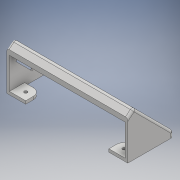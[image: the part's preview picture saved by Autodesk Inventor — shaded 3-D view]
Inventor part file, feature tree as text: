
AUTODESK INVENTOR PART (.ipt)
format: ipt  version: 2018 (Build 220112000, 112)  size: 429,056 bytes
history: native  units: mm
features: extrude x10, sketch x10, projected_geometry x3, fillet x2, chamfer x1, mirror x1, emboss x1
ambient origin geometry x8: Origin, YZ Plane, XZ Plane, XY Plane, X Axis, Y Axis, Z Axis, Center Point
bodies: Solid1 (feature_tree)
feature tree (28):
  extrude  "Extrusion1"  Depth=73.0mm
  extrude  "Extrusion2"  Depth=60.0mm
  extrude  "Extrusion3"  Depth=7.0mm
  fillet  "Fillet1"  Radius=3.5mm
  extrude  "Extrusion4"  Depth=3.5mm
  extrude  "Extrusion5"  Depth=120.0mm TaperAngle=0.0deg
  extrude  "Extrusion6"  Depth=40.5mm
  chamfer  "Chamfer1"  Distance=11.0mm
  extrude  "Extrusion7"  Depth=10.0mm TaperAngle=0.0deg
  sketch  "Sketch8"  dims[d19=26.4mm]
  fillet  "Fillet2"  Radius=3.0mm
  extrude  "Extrusion8"  Depth=10.0mm TaperAngle=0.0deg
  mirror  "Mirror1"
  emboss  "Emboss1"
  extrude  "Extrusion9"  Depth=10.0mm
  extrude  "Extrusion10"  Depth=10.0mm
  sketch  "Sketch1"  dims[d3=8.726646mm d4=73.0mm]
  sketch  "Sketch2"  dims[d6=160.0mm d7=0.0mm d8=60.0mm]
  sketch  "Sketch3"  dims[d9=45.0deg d10=7.0mm d11=3.5mm]
  projected_geometry  "Projected Loop1"
  sketch  "Sketch4"  dims[d12=3.5mm d13=3.5mm]
  projected_geometry  "Projected Loop2"
  sketch  "Sketch5"  dims[d14=3.5mm d15=120.0mm d16=0.0mm]
  projected_geometry  "Projected Loop3"
  sketch  "Sketch7"  dims[d17=98.5mm d18=40.5mm]
  sketch  "Sketch9"  dims[d20=12.5mm]
  sketch  "Sketch10"  dims[d21=22.7mm]
  sketch  "Sketch11"  dims[d22=15.2mm d23=11.0mm d30=3.0mm d31=0.0mm d32=3.0mm d33=3.0mm d34=0.0mm d35=30.0mm d36=6.0mm d37=3.0mm d38=0.0mm d39=14.5mm d40=15.0mm d41=3.2mm d42=144.5mm d43=49.5mm d44=3.6mm d45=11.2mm d46=3.0mm d47=0.0mm d48=2.0mm d49=2.0mm d50=45.0deg d51=25.0mm d52=20.0mm d53=4.0mm d54=0.0mm d55=10.0mm d56=10.0mm d57=4.2mm d58=10.0mm d59=4.0mm d60=0.0mm d61=1.0mm d62=0.0mm d63=10.0mm d64=0.0mm d65=0.0mm d66=0.0mm d67=13.0mm d69=0.5mm d70=19.0mm]
